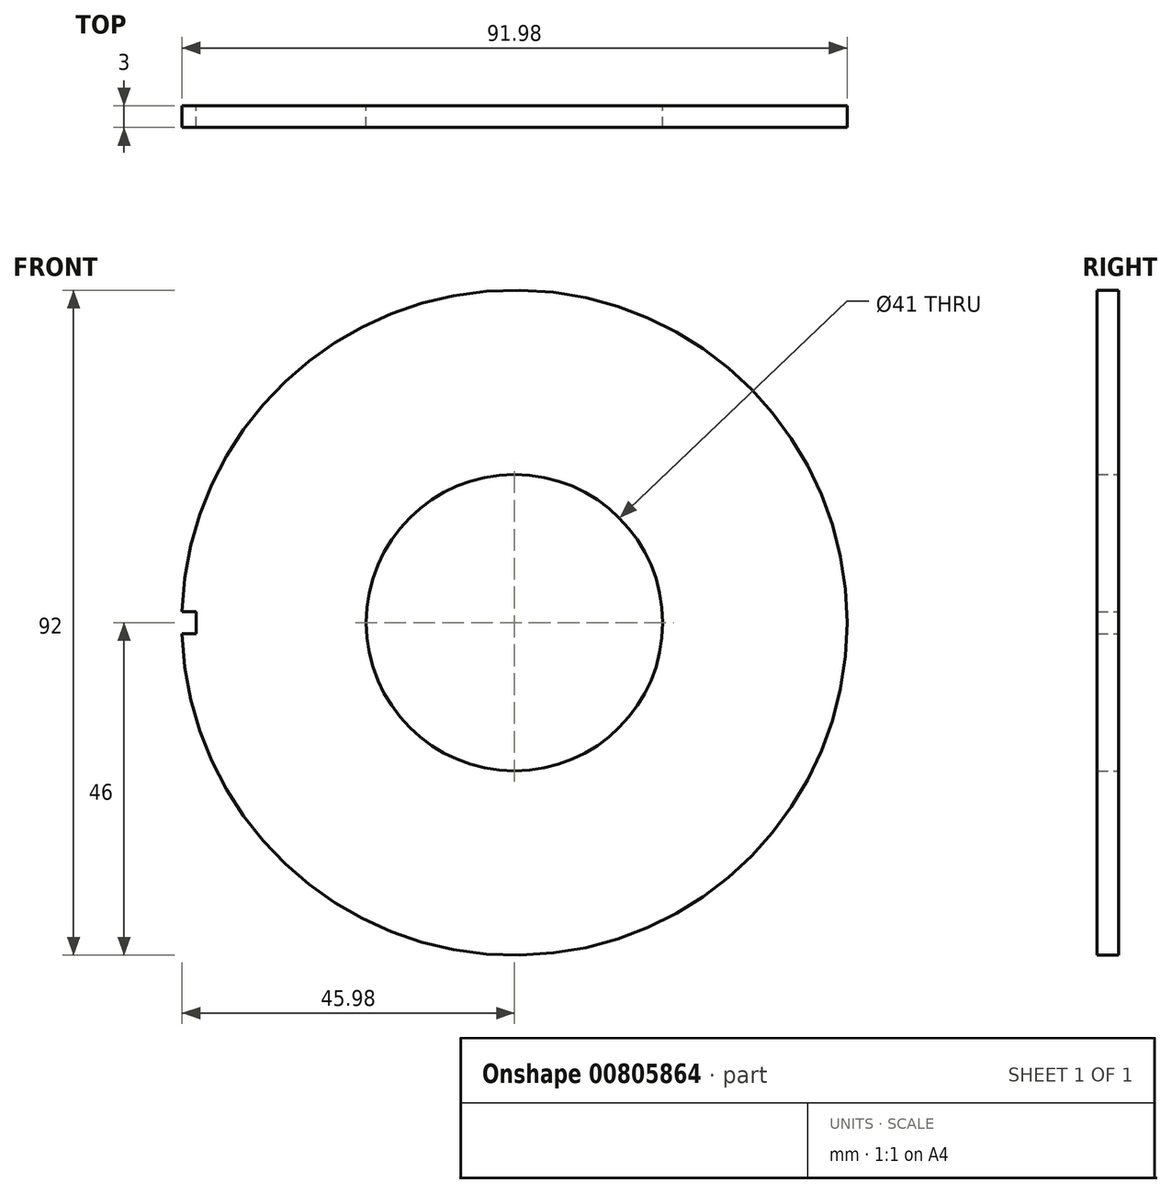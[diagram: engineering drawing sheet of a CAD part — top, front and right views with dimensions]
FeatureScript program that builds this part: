
annotation { "Feature Type Name" : "Feature", "Feature Type Description" : "" }
export const myFeature = defineFeature(function(context is Context, id is Id, definition is map)
    precondition{}
    {
        {
            var Q0;
            Q0=qCreatedBy(makeId("Front.planeOp"),FACE);
            var sketch = newSketch(context, id + "F0", { "sketchPlane" : qUnion([Q0])});
            skCircle(sketch, "E0", {"center": v(0, 0) * mm, "radius": 20.5 * mm});
            skCircle(sketch, "E1", {"center": v(0, 0) * mm, "radius": 46 * mm});
            skSolve(sketch);
        }
        {
            var Q0;
            Q0=makeQuery(id+"F0.imprint","IMPRINT",FACE,{"disambiguationData":[TD([[makeQuery(id+"F0.imprint","IMPRINT",EDGE,{"derivedFrom":sQuery(id+"F0.wireOp",EDGE,"E0")}),-1.0]])]});
            extrude(context, id + "F1", {"entities" : qUnion([Q0]), "depth" : 3 * mm, "offsetDistance" : 25 * mm});
        }
        {
            var Q0;
            Q0=qCreatedBy(makeId("Front.planeOp"),FACE);
            var sketch = newSketch(context, id + "F2", { "sketchPlane" : qUnion([Q0])});
            skLineSegment(sketch, "E2.bottom", {"start": v(-44, -1.5) * mm, "end": v(-46, -1.5) * mm});
            skLineSegment(sketch, "E2.top", {"start": v(-44, 1.5) * mm, "end": v(-46, 1.5) * mm});
            skLineSegment(sketch, "E2.left", {"start": v(-44, -1.5) * mm, "end": v(-44, 1.5) * mm});
            skLineSegment(sketch, "E2.right", {"start": v(-46, -1.5) * mm, "end": v(-46, 1.5) * mm});
            skPoint(sketch, "E2.middle", {"position": v(-45, 0) * mm});
            skSolve(sketch);
        }
        {
            var Q0;
            Q0=qSketchRegion(id+"F2",true);
            extrude(context, id + "F3", {"entities" : qUnion([Q0]), "operationType" : NewBodyOperationType.REMOVE, "depth" : 3 * mm, "offsetDistance" : 25 * mm});
        }
    });
